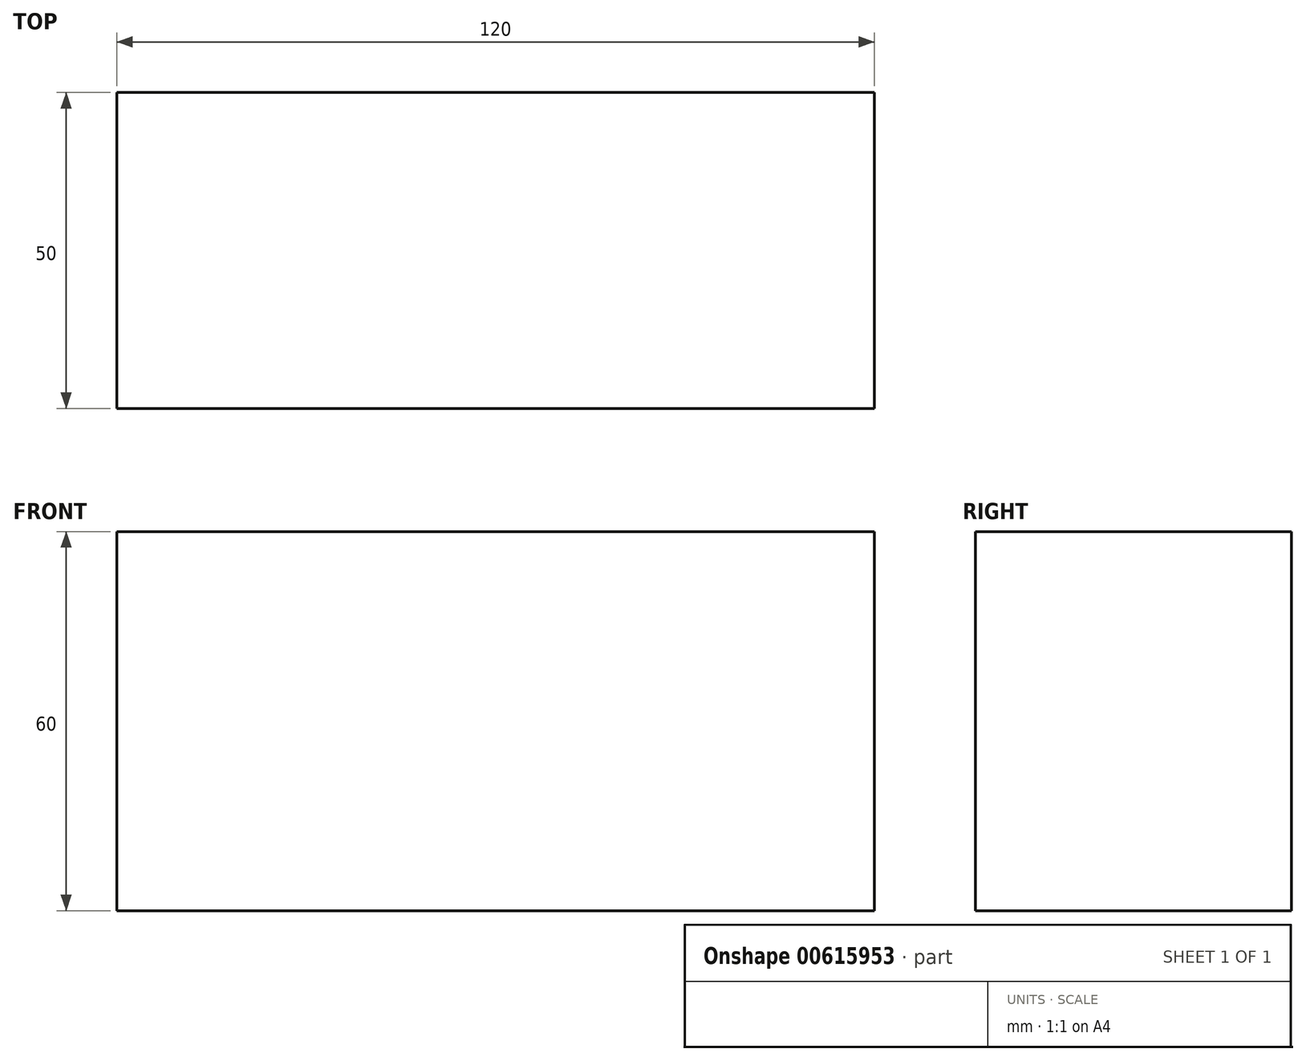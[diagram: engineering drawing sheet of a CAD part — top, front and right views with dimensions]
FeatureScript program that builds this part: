
annotation { "Feature Type Name" : "Feature", "Feature Type Description" : "" }
export const myFeature = defineFeature(function(context is Context, id is Id, definition is map)
    precondition{}
    {
        {
            var Q0;
            Q0=qCreatedBy(makeId("Front.planeOp"),FACE);
            var sketch = newSketch(context, id + "F0", { "sketchPlane" : qUnion([Q0])});
            skLineSegment(sketch, "E0.bottom", {"start": v(0, 0) * mm, "end": v(120, 0) * mm});
            skLineSegment(sketch, "E0.top", {"start": v(0, 60) * mm, "end": v(120, 60) * mm});
            skLineSegment(sketch, "E0.left", {"start": v(0, 0) * mm, "end": v(0, 60) * mm});
            skLineSegment(sketch, "E0.right", {"start": v(120, 0) * mm, "end": v(120, 60) * mm});
            skSolve(sketch);
        }
        {
            var Q0;
            Q0 = qSketchRegion(id + "F0", true);
            extrude(context, id + "F1", {"entities" : qUnion([Q0]), "depth" : 50 * mm, "offsetDistance" : 25 * mm});
        }
    });
